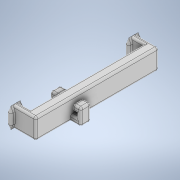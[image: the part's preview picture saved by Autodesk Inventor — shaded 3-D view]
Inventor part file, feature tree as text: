
AUTODESK INVENTOR PART (.ipt)
format: ipt  version: 2020 (Build 240168000, 168)  size: 281,600 bytes
history: native  units: in
note: dims shown in document units (in); Inventor stores cm internally (conversion verified against a paired STEP export)
features: extrude x5, sketch x5, fillet x2, chamfer x2, mirror x2, plane x1, boolean_combine x1, projected_geometry x1
ambient origin geometry x8: Origin, YZ Plane, XZ Plane, XY Plane, X Axis, Y Axis, Z Axis, Center Point
bodies: Solid1 (feature_tree), Solid2 (feature_tree)
feature tree (19):
  extrude  "Extrusion1"  Depth=0.1969in
  extrude  "Extrusion2"  Depth=0.0787in
  extrude  "Extrusion3"  Depth=0.0787in
  extrude  "Extrusion4"  Depth=0.3937in
  fillet  "Fillet3"  Radius=0.3937in
  chamfer  "Chamfer1"  Distance=0.0394in Angle=45.0deg
  chamfer  "Chamfer2"  Distance=0.0394in Angle=45.0deg
  mirror  "Mirror1"
  fillet  "Fillet4"  Radius=0.125in
  plane  "Work Plane1"
  mirror  "Mirror2"
  boolean_combine  "Combine1"
  extrude  "Extrusion5"  Depth=0.1969in
  sketch  "Sketch1"  dims[d1=0.0984in d2=0.1969in]
  sketch  "Sketch2"  dims[d3=0.2in d4=0.0787in]
  sketch  "Sketch3"  dims[d5=0.0787in d6=0.0787in]
  sketch  "Sketch4"  dims[d7=0.0394in d8=1.0827in d9=0.3937in d10=0.0in]
  sketch  "Sketch5"  dims[d13=0.0394in d14=0.0394in d15=0.0984in d16=45.0deg d17=0.0394in d18=0.0984in d19=45.0deg d20=0.125in d21=0.1969in d22=0.1181in d23=0.1969in d24=0.0in d25=0.0787in d26=0.1969in d27=0.0in d28=0.1181in d29=0.0787in d30=0.0in d31=0.6664in d32=0.0787in d33=0.0in]
  projected_geometry  "Projected Loop1"
